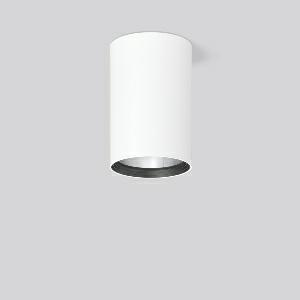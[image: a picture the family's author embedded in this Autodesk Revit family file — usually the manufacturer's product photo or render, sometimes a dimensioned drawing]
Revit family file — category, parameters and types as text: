
# Revit family: heledon_maxi_a_931233_002_4826
name_source: partatom
category: Lighting Fixtures
units: mm (PartAtom-declared; Revit-internal decimal feet)

## family parameters
Cut with Voids When Loaded = No
Host = Face
Light Source = No
Part Type = Normal
Room Calculation Point = No
Round Connector Dimension = Use Diameter
Shared = No

## types (1)
- HELEDON maxi A (1 x LED Modul 932 fresh meat, 2050 lm, 3200)
    Apparent Load = 33 VA
    Approval mark = CE
    CIE Flux Codes = 96 100 100 100 100
    Color Rendering = 90
    Color Temperature = 3200
    Default Elevation = 1800 mm
    Description = Series: HELEDON maxi
Cylindrical surface-mounted downlight. Housing: die-cast aluminium, powder-coated. Internal ceiling frame polycarbonate with bayonet mounting. Black plastic ring and recessed LED to prevent glare from the side. Optical assembly with reflector made of MIRO-Silver with 98% total light reflection for outstanding efficiency - can be changed without tools. Special LED for illumination of meat included. Suitable for Ceiling mounting. Easy installation with a separate ceiling frame with bayonet mounting and plug connection. Driver integrated. Connected via plug-in connector. High quality converter without flickering and stroboscopic effect. The following accessories can be mounted without use of tools: interchangeable lenses, decorative glasses, honeycomb louvre, clear and frosted diffusers, white interchangeable plastic ring. 
Colour: traffic white, matt (RAL 9016)
Diameter: 123 mm
Height: 183 mm
Lamp: LED
Socket: without socket
Colour temperature: fresh meat
System power: 33 W
Rated luminous flux: 2050 lm
Luminous efficiency: 62 lm/W
Control gear: Regulated power supply
Protection class: I
Type of protection: IP 20
    Height = 183 mm
    Lamp = 1 x LED Modul 932 fresh meat
    Lamp Light Flux = 2050 lm
    Lamp count = 1
    Length = 123 mm
    Lifetime = 50000 h
    Luminous efficacy = 62 lm/W
    Manufacturer = RZB
    ModVariant = No
    Model = 931233.002
    Mounting Place = Ceiling
    Mounting Type = Surface mounted
    Number of Poles = 1
    OnlyDefault = Yes
    Power Factor = 1
    Product Name = HELEDON maxi A
    Product group = Surface mounted downlights
    ProductGroupID = 302
    Protection Class = Protection class I
    Protection Degree = IP 20
    RLX_Detail_Level = 1
    RLX_Emergency_Light_Flux = 0 lm
    RLX_Emergency_Type = 0
    RLX_Emergency_Type_DB = No
    RlxData = <blob elided: 97669 chars, md5=306002df>
    Socket = socket
    Standby Power = 0 W
    System Light Flux = 2050 lm
    System Power = 33 W
    Type Comments = Product without accessories
    Type Image = 931192.002.jpg
    URL = http://relux.com
    VarID = ---
    Voltage = 230 V
    Voltage Range = 220-240 V
    Weight = 0.00 kg
    Width = 0 mm  [stored 0 ft]

note: [stored X ft] marks values corroborated as IEEE doubles in the binary element streams (Revit-internal decimal feet)

## geometry (parser evidence)
native form markers: Blend x4, Sweep x9
no freeform markers — native parametric forms only
